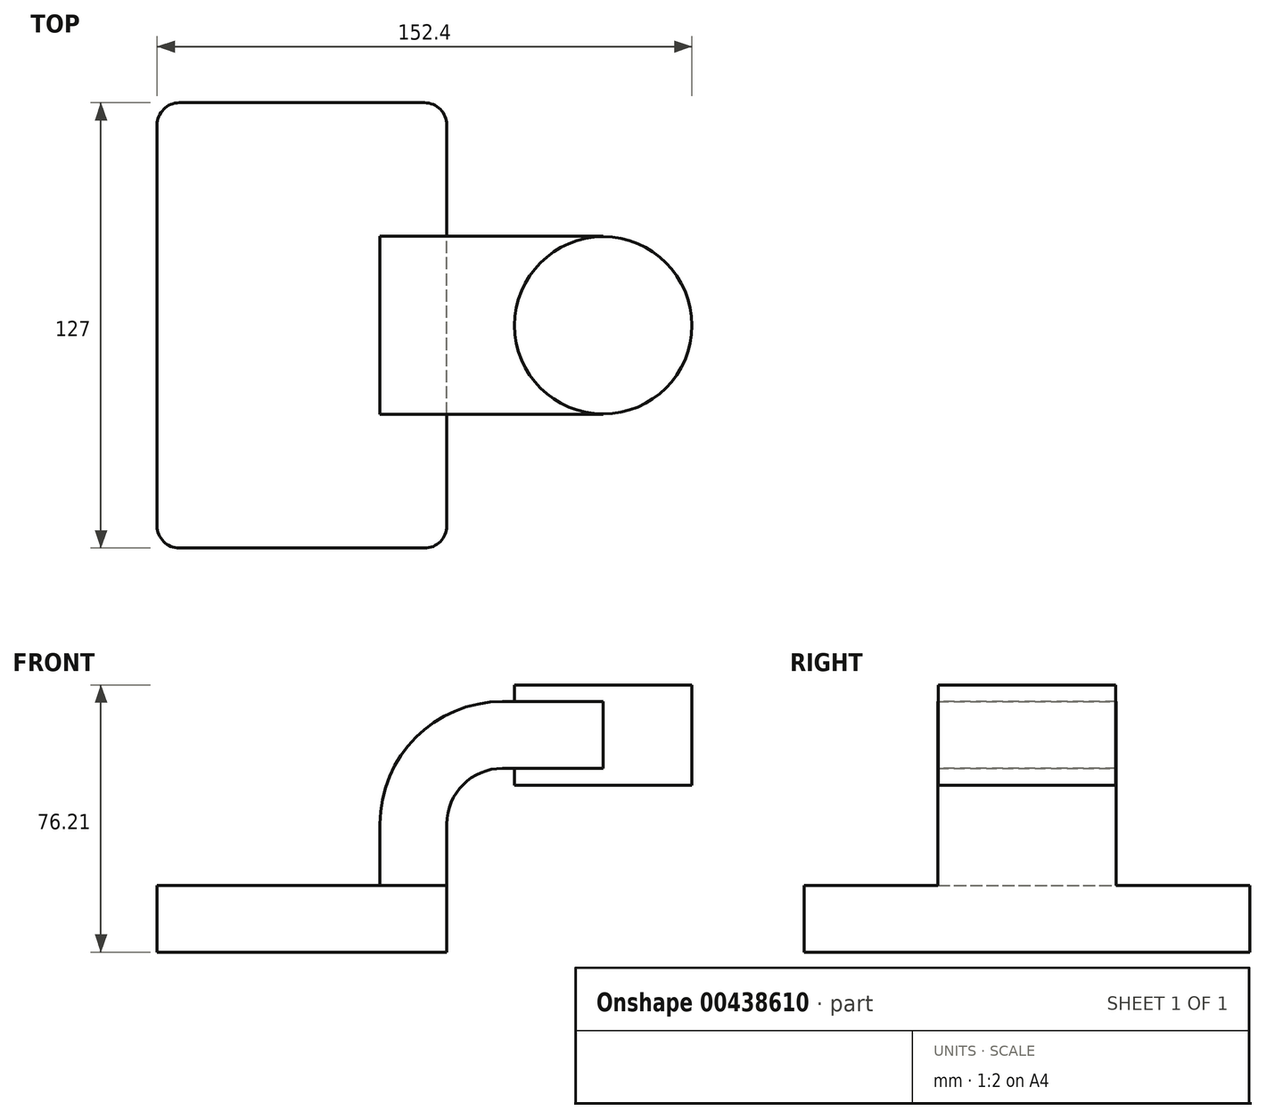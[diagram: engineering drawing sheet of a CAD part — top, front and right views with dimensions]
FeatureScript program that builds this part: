
annotation { "Feature Type Name" : "Feature", "Feature Type Description" : "" }
export const myFeature = defineFeature(function(context is Context, id is Id, definition is map)
    precondition{}
    {
        {
            var Q0;
            Q0=qCreatedBy(makeId("Front.planeOp"),FACE);
            var sketch = newSketch(context, id + "F0", { "sketchPlane" : qUnion([Q0])});
            skLineSegment(sketch, "E0.bottom", {"start": v(-41.28, 9.52) * mm, "end": v(41.27, 9.53) * mm});
            skLineSegment(sketch, "E0.top", {"start": v(-41.28, -9.53) * mm, "end": v(41.28, -9.53) * mm});
            skLineSegment(sketch, "E0.left", {"start": v(-41.28, 9.52) * mm, "end": v(-41.27, -9.53) * mm});
            skLineSegment(sketch, "E0.right", {"start": v(41.28, 9.53) * mm, "end": v(41.28, -9.52) * mm});
            skPoint(sketch, "E0.middle", {"position": v(0, 0) * mm});
            skLineSegment(sketch, "E1.bottom", {"start": v(60.33, 38.1) * mm, "end": v(111.12, 38.1) * mm});
            skLineSegment(sketch, "E1.top", {"start": v(60.32, 66.67) * mm, "end": v(111.12, 66.67) * mm});
            skLineSegment(sketch, "E1.left", {"start": v(60.33, 38.1) * mm, "end": v(60.32, 66.68) * mm});
            skLineSegment(sketch, "E1.right", {"start": v(111.12, 38.1) * mm, "end": v(111.12, 66.68) * mm});
            skPoint(sketch, "E1.middle", {"position": v(85.72, 52.39) * mm});
            skLineSegment(sketch, "E2", {"start": v(41.27, 9.53) * mm, "end": v(41.27, 27) * mm});
            skArc(sketch, "E3", {"start": v(41.27, 27) * mm, "mid": v(45.92, 38.23) * mm, "end": v(57.15, 42.88) * mm});
            skLineSegment(sketch, "E4", {"start": v(57.15, 42.88) * mm, "end": v(85.85, 42.88) * mm});
            skLineSegment(sketch, "E5.0", {"start": v(57.15, 61.93) * mm, "end": v(85.85, 61.93) * mm});
            skArc(sketch, "E5.1", {"start": v(22.23, 27) * mm, "mid": v(32.45, 51.7) * mm, "end": v(57.15, 61.93) * mm});
            skLineSegment(sketch, "E5.2", {"start": v(22.23, 9.53) * mm, "end": v(22.23, 27) * mm});
            skLineSegment(sketch, "E6", {"start": v(85.85, 42.88) * mm, "end": v(85.85, 61.93) * mm});
            skFitSpline(sketch, "E7", {"points": [v(-41.28, 9.53) * mm, v(57.15, 61.93) * mm], "startDerivative": vector(0.26, 61.02) * mm, "endDerivative": vector(136.98, -0.57) * mm});
            skLineSegment(sketch, "E8", {"start": v(85.85, 61.93) * mm, "end": v(85.85, 66.67) * mm});
            skLineSegment(sketch, "E9", {"start": v(85.85, 66.67) * mm, "end": v(85.85, 38.1) * mm});
            skSolve(sketch);
        }
        {
            var Q0;
            Q0=makeQuery(id+"F0.imprint","IMPRINT",FACE,{"disambiguationData":[TD([[makeQuery(id+"F0.imprint","IMPRINT",EDGE,{"derivedFrom":sQuery(id+"F0.wireOp",EDGE,"E0.top")}),1.0]])]});
            extrude(context, id + "F1", {"entities" : qUnion([Q0]), "endBound" : BoundingType.SYMMETRIC, "depth" : 127 * mm});
        }
        {
            var Q0;
            {var subQ1=sQuery(id+"F0.wireOp",EDGE,"E2");Q0=makeQuery(id+"F0.imprint","IMPRINT",FACE,{"disambiguationData":[TD([[makeQuery(id+"F0.imprint","IMPRINT",EDGE,{"derivedFrom":subQ1}),1.0]])]});}
            var Q1;
            {var subQ0=sQuery(id+"F0.wireOp",EDGE,"E4");var subQ1=sQuery(id+"F0.wireOp",EDGE,"E1.left");var subQ2=makeQuery(id+"F0.imprint","INTERSECT",VERTEX,{"derivedFrom":[subQ1,subQ0]});Q1=makeQuery(id+"F0.imprint","IMPRINT",FACE,{"disambiguationData":[TD([[makeQuery(id+"F0.imprint","IMPRINT",EDGE,{"disambiguationData":[TD([[subQ2,-1.0]])],"derivedFrom":subQ1}),-1.0]])]});}
            extrude(context, id + "F2", {"entities" : qUnion([Q0, Q1]), "operationType" : NewBodyOperationType.ADD, "endBound" : BoundingType.SYMMETRIC, "depth" : 50.8 * mm});
        }
        {
            var Q0;
            Q0=makeQuery(id+"F0.imprint","IMPRINT",FACE,{"disambiguationData":[TD([[makeQuery(id+"F0.imprint","IMPRINT",EDGE,{"derivedFrom":sQuery(id+"F0.wireOp",EDGE,"E5.1")}),1.0]])]});
            extrude(context, id + "F3", {"entities" : qUnion([Q0]), "operationType" : NewBodyOperationType.ADD, "endBound" : BoundingType.SYMMETRIC, "depth" : 15.88 * mm});
        }
        {
            var Q0;
            {var subQ4=sQuery(id+"F0.wireOp",EDGE,"E1.right");Q0=makeQuery(id+"F0.imprint","IMPRINT",FACE,{"disambiguationData":[TD([[makeQuery(id+"F0.imprint","IMPRINT",EDGE,{"derivedFrom":subQ4}),1.0]])]});}
            var Q1;
            Q1=sQuery(id+"F0.wireOp",EDGE,"E9");
            revolve(context, id + "F4", {"operationType" : NewBodyOperationType.ADD, "entities" : qUnion([Q0]), "axis" : qUnion([Q1]), "revolveType" : RevolveType.FULL});
        }
        {
            var Q0;
            Q0=makeQuery(id+"F1.opExtrude","CAP_EDGE",EDGE,{"disambiguationData":[OSD([sQuery(id+"F0.wireOp",EDGE,"E0.right")])],"isStart":false});
            var Q1;
            Q1=makeQuery(id+"F1.opExtrude","CAP_EDGE",EDGE,{"disambiguationData":[OSD([sQuery(id+"F0.wireOp",EDGE,"E0.left")])],"isStart":false});
            var Q2;
            Q2=makeQuery(id+"F1.opExtrude","CAP_EDGE",EDGE,{"disambiguationData":[OSD([sQuery(id+"F0.wireOp",EDGE,"E0.left")])],"isStart":true});
            var Q3;
            Q3=makeQuery(id+"F1.opExtrude","CAP_EDGE",EDGE,{"disambiguationData":[OSD([sQuery(id+"F0.wireOp",EDGE,"E0.right")])],"isStart":true});
            fillet(context, id + "F5", {"entities" : qUnion([Q0, Q1, Q2, Q3]), "radius" : 6.35 * mm, "tangentPropagation" : true, "allowEdgeOverflow" : false});
        }
    });
